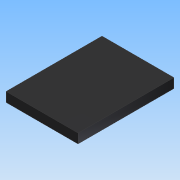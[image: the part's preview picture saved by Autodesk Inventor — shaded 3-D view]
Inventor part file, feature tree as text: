
AUTODESK INVENTOR PART (.ipt)
format: ipt  version: 2015 (Build 190159000, 159)  size: 74,240 bytes
history: native  units: mm
features: extrude x1, sketch x1
ambient origin geometry x8: Origin, YZ Plane, XZ Plane, XY Plane, X Axis, Y Axis, Z Axis, Center Point
bodies: Volumenkörper1 (feature_tree)
feature tree (2):
  extrude  "Extrusion1"  Depth=20.32mm
  sketch  "Skizze1"  dims[d0=15.24mm d1=20.32mm d2=2.0mm d3=0.0mm]
